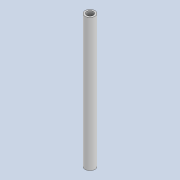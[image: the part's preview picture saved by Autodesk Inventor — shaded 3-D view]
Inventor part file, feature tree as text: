
AUTODESK INVENTOR PART (.ipt)
format: ipt  version: 2020 (Build 240168000, 168)  size: 73,216 bytes
history: native  units: mm
features: extrude x1, sketch x1
ambient origin geometry x8: Origin, YZ Plane, XZ Plane, XY Plane, X Axis, Y Axis, Z Axis, Center Point
bodies: Solid1 (feature_tree)
feature tree (2):
  extrude  "Extrusion1"  Depth=40.0mm
  sketch  "Sketch1"  dims[d0=3.0mm d1=0.5mm d2=40.0mm d3=0.0mm]
